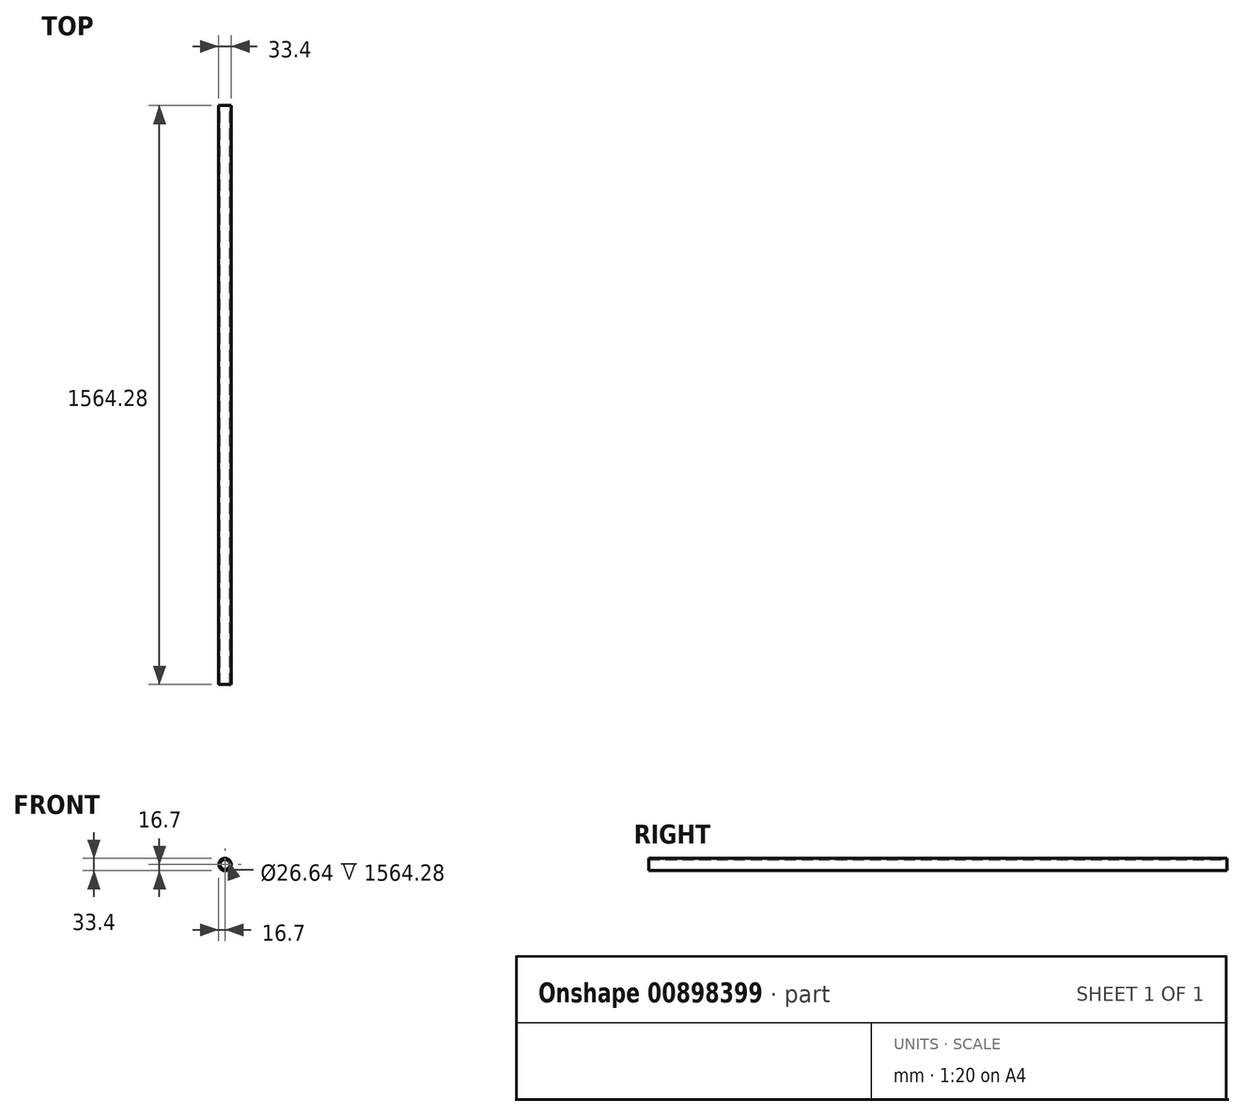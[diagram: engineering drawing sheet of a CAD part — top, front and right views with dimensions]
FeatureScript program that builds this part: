
annotation { "Feature Type Name" : "Feature", "Feature Type Description" : "" }
export const myFeature = defineFeature(function(context is Context, id is Id, definition is map)
    precondition{}
    {
        {
            var Q0;
            Q0=qCreatedBy(makeId("Front.planeOp"),FACE);
            var sketch = newSketch(context, id + "F0", { "sketchPlane" : qUnion([Q0])});
            skCircle(sketch, "E0", {"center": v(0, 0) * mm, "radius": 16.7 * mm});
            skCircle(sketch, "E1", {"center": v(0, 0) * mm, "radius": 13.32 * mm});
            skSolve(sketch);
        }
        {
            var Q0;
            Q0=makeQuery(id+"F0.imprint","IMPRINT",FACE,{"disambiguationData":[TD([[makeQuery(id+"F0.imprint","IMPRINT",EDGE,{"derivedFrom":sQuery(id+"F0.wireOp",EDGE,"E0")}),1.0]])]});
            extrude(context, id + "F1", {"entities" : qUnion([Q0]), "endBound" : BoundingType.SYMMETRIC, "depth" : 1564.28 * mm, "offsetDistance" : 25.4 * mm});
        }
    });
